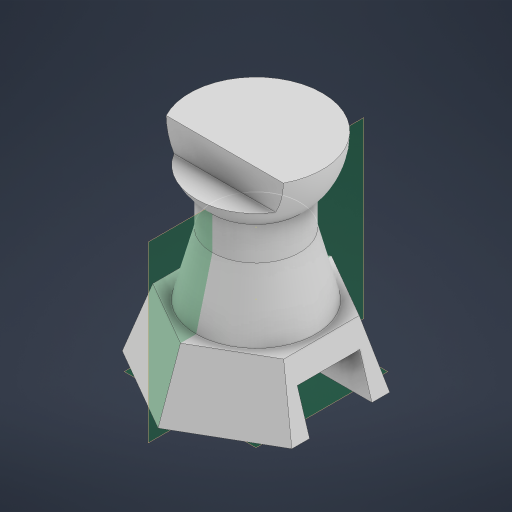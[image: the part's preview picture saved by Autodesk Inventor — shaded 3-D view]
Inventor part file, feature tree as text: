
AUTODESK INVENTOR PART (.ipt)
format: ipt  version: 2024.3 (Build 283343000, 343)  size: 267,776 bytes
history: native  units: mm
features: sketch x10, plane x3, loft x3, extrude x2, revolve x1, other x1
ambient origin geometry x8: Origin, YZ Plane, XZ Plane, XY Plane, X Axis, Y Axis, Z Axis, Center Point
bodies: Solid1 (feature_tree)
feature tree (20):
  extrude  "Extrusion1"  Depth=16.0mm TaperAngle=0.0deg
  sketch  "Sketch3"  dims[d4=42.0mm d5=30.0mm]
  plane  "Work Plane1"
  loft  "Loft1"
  sketch  "Sketch5"  dims[d12=30.0mm d17=0.0mm d18=90.0deg]
  plane  "Work Plane2"
  sketch  "Sketch6"  dims[d19=0.0mm d20=90.0deg d30=0.0mm d31=90.0deg]
  loft  "Loft3"
  loft  "Loft4"
  plane  "Work Plane4"
  revolve  "Revolution1"  Angle=90.0deg
  extrude  "Extrusion2"  TaperAngle=90.0deg  [1 undecoded]
  sketch  "Sketch2"  dims[d1=42.0mm d2=16.0mm d3=0.0mm]
  sketch  "Sketch4"  dims[d6=57.54mm d7=0.0mm d8=90.0deg d9=0.0mm d10=90.0deg]
  other  "Edges1"
  sketch  "Sketch8"  dims[d32=0.0mm d33=90.0deg d38=90.0deg]
  sketch  "Sketch9"  dims[d40=15.0mm]
  sketch  "Sketch10"  dims[d41=20.0mm]
  sketch  "Sketch12"  dims[d42=30.0mm]
  sketch  "Sketch14"  dims[d47=14.0mm d48=90.0deg d49=90.0deg d50=70.0mm d51=0.0mm]
note: 1 required parameter value undecoded (feature->parameter linkage not recoverable at this tier; creation-order binding heuristic only, values carry confidence <= 0.55)
